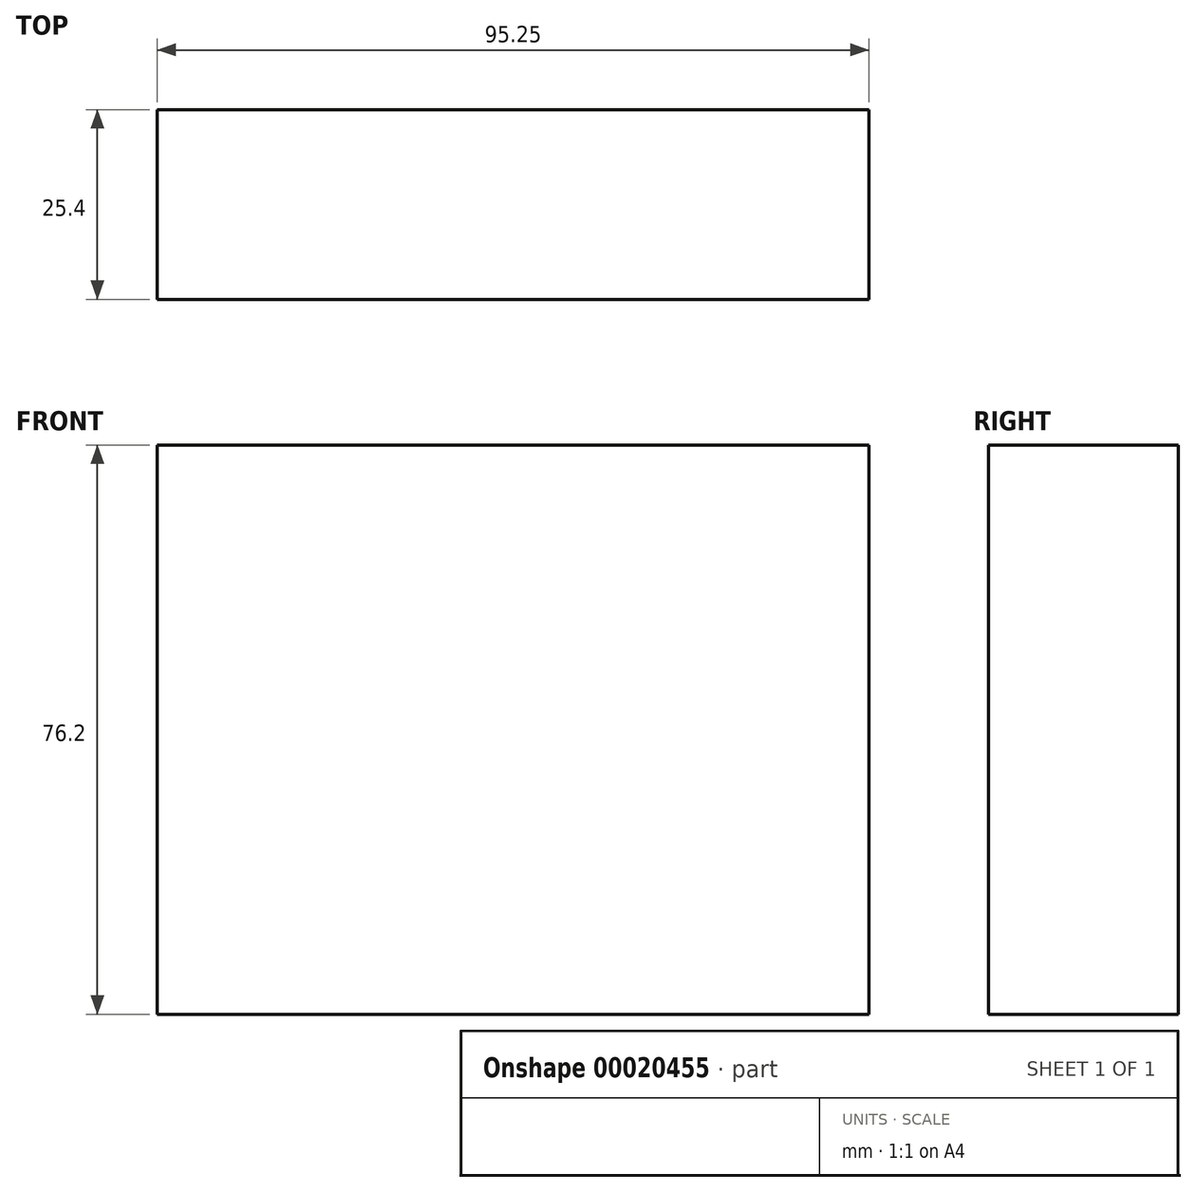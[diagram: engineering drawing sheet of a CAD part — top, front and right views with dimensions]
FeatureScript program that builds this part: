
annotation { "Feature Type Name" : "Feature", "Feature Type Description" : "" }
export const myFeature = defineFeature(function(context is Context, id is Id, definition is map)
    precondition{}
    {
        {
            var Q0;
            Q0=qCreatedBy(makeId("Front.planeOp"),FACE);
            var sketch = newSketch(context, id + "F0", { "sketchPlane" : qUnion([Q0])});
            skLineSegment(sketch, "E0.bottom", {"start": v(-53.08, 37.93) * mm, "end": v(42.17, 37.93) * mm});
            skLineSegment(sketch, "E0.top", {"start": v(-53.08, -38.27) * mm, "end": v(42.17, -38.27) * mm});
            skLineSegment(sketch, "E0.left", {"start": v(-53.08, 37.93) * mm, "end": v(-53.08, -38.27) * mm});
            skLineSegment(sketch, "E0.right", {"start": v(42.17, 37.93) * mm, "end": v(42.17, -38.27) * mm});
            skLineSegment(sketch, "E1.bottom", {"start": v(42.17, 9.35) * mm, "end": v(42.17, 9.35) * mm});
            skLineSegment(sketch, "E1.top", {"start": v(42.17, 14.01) * mm, "end": v(42.17, 14.01) * mm});
            skLineSegment(sketch, "E1.left", {"start": v(42.17, 9.35) * mm, "end": v(42.17, 14.01) * mm});
            skLineSegment(sketch, "E1.right", {"start": v(42.17, 9.35) * mm, "end": v(42.17, 14.01) * mm});
            skSolve(sketch);
        }
        {
            var Q0;
            Q0 = qSketchRegion(id + "F0", true);
            extrude(context, id + "F1", {"entities" : qUnion([Q0]), "depth" : 25.4 * mm});
        }
    });
